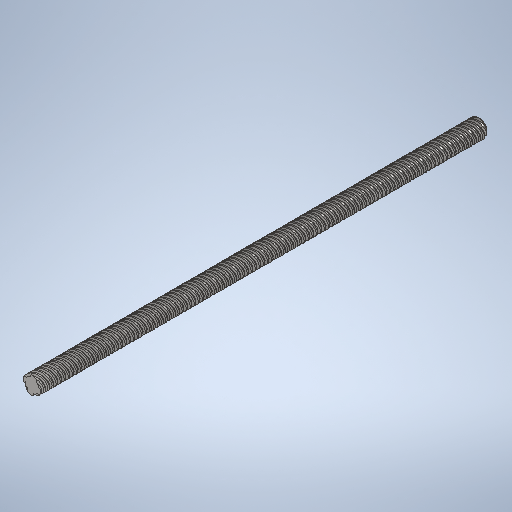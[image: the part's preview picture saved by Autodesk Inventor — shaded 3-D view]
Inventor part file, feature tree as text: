
AUTODESK INVENTOR PART (.ipt)
format: ipt  version: 2025.2 (Build 292293000, 293)  size: 1,708,544 bytes
history: native  units: mm
features: extrude x2, chamfer x1, other x1, pattern_circular x1, sketch x1
ambient origin geometry x8: Origin, YZ Plane, XZ Plane, XY Plane, X Axis, Y Axis, Z Axis, Center Point
bodies: Solid1 (feature_tree)
feature tree (6):
  extrude  "1000mm Rod"  Depth=0.907143mm TaperAngle=45.0deg
  chamfer  "Chamfer1"  Distance=7.257143mm
  other  "ACME Thread 2mm Pitch"
  pattern_circular  "4 Start"  Count=4 Angle=360.0deg
  extrude  "Extrusion2"  Depth=1.814286mm
  sketch  "Sketch3"  dims[d1=1000.0mm d2=0.0mm d3=0.907143mm d4=2.0mm d5=45.0deg d14=7.257143mm d15=1001.814286mm d16=10.0mm d17=0.0mm d18=90.0deg d19=90.0deg d20=0.0mm d21=0.0mm d40=40.0mm d41=360.0deg d43=1.814286mm d44=0.907143mm d48=5.061455mm d49=8.0mm d50=800.0mm d51=0.0mm]
